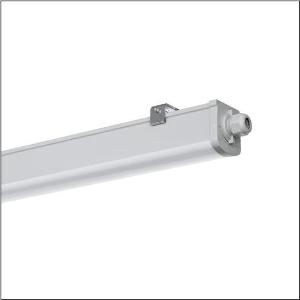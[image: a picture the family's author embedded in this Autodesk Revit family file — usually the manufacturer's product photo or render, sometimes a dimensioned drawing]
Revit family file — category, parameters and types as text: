
# Revit family: monsun_r__31_51fa207d420b_180d
name_source: partatom
category: Lighting Fixtures
units: mm (PartAtom-declared; Revit-internal decimal feet)

## family parameters
Cut with Voids When Loaded = No
Host = Face
Light Source = No
Part Type = Normal
Room Calculation Point = No
Round Connector Dimension = Use Diameter
Shared = No

## types (1)
- Monsun® 31 (1 x LED, 2300 lm, 19 W, 4000K)
    Apparent Load = 19 VA
    CIE Flux Codes = 42 72 91 92 100
    Color Rendering = 80
    Color Temperature = 4000K
    Default Elevation = 1800 mm
    Description = Monsun® 31, damp-proof luminaire, primary optical cover: diffuser, of PC, frosted, light emission: direct distribution, primary light characteristic: symmetric, installation type: surface-mounted, LED, rated luminous flux: 2.300lm, luminous efficacy: 121lm/W, light colour: 840, colour temperature: 4000K, control gear: ECG, with terminal, 3+1-pole, max. 2.5mm², through-wiring: 3x 2.5mm² + 1x 1.5mm², mains connection: 220..240V, AC, 50/60Hz, rated input power: 19W, housing, luminaire housing, of PC, light grey (RAL 7035), length: 558mm, width: 68mm, height: 76mm, protection rating (complete): IP66, insulation class (complete): insulation class II (safety insulation), certification: CE, ENEC, UKCA, protection symbol: D, impact resistance: IK08, permissible operating ambient temperature: -20..+40°C, corresponds to IFS (International Featured Standards) requirements for safety and quality in the food industry, contact your sales advisor before using the luminaires in applications with unclear chemical exposure, large temperature fluctuations or condensation-forming humidity, packaging unit: 1 piece
    Height = 77 mm
    Lamp = 1 x LED
    Lamp Light Flux = 2300 lm
    Lamp Power = 19 W
    Lamp count = 1
    Length = 618 mm
    Luminous efficacy = 121 lm/W
    Manufacturer = Siteco
    ModVariant = No
    Model = 51FA207D420B
    Mounting Place = Ceiling
    Mounting Type = Surface mounted
    Number of Poles = 1
    OnlyDefault = Yes
    Power Factor = 1
    Product Name = Monsun® 31
    Product group = damp-proof luminaire
    ProductGroupID = 300
    Protection Class = Protection class II
    Protection Degree = IP 66
    RLX_Detail_Level = 1
    RLX_Emergency_Light_Flux = 0 lm
    RLX_Emergency_Type = 0
    RLX_Emergency_Type_DB = No
    RlxData = <blob elided: 32889 chars, md5=b8491535>
    Socket = socket
    Standby Power = 0 W
    System Light Flux = 2300 lm
    System Power = 19 W
    Type Comments = Product without accessories
    Type Image = l_1006174.jpg
    URL = http://relux.com
    VarID = ---
    Voltage = 0 V
    Weight = 0.00 kg
    Width = 69 mm

## geometry (parser evidence)
native form markers: Blend x4, Sweep x14
no freeform markers — native parametric forms only
